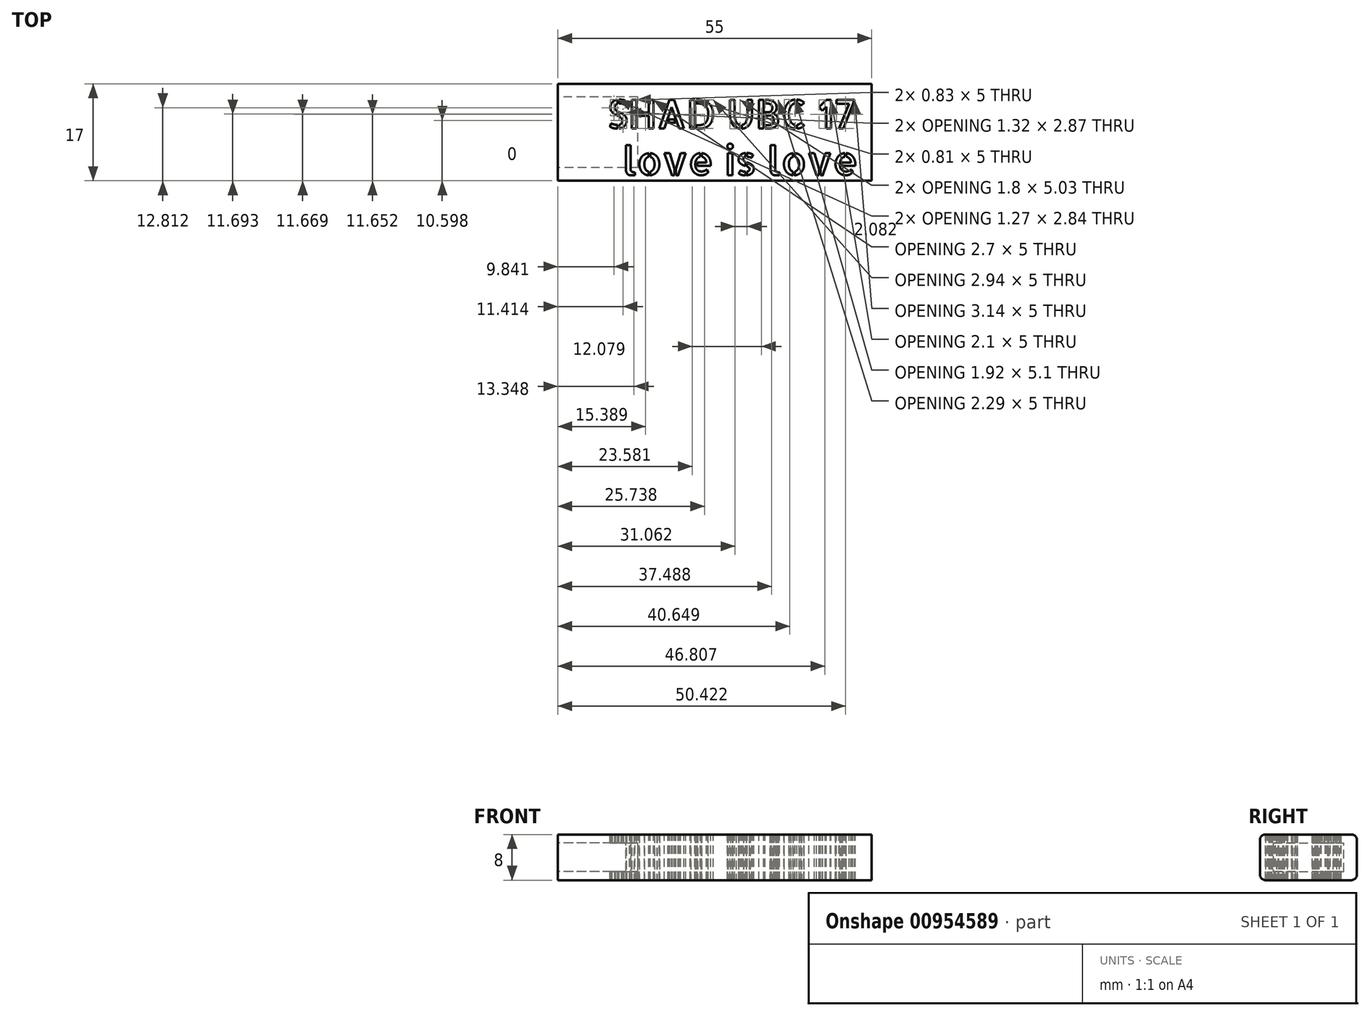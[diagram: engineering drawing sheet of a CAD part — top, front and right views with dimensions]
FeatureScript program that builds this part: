
annotation { "Feature Type Name" : "Feature", "Feature Type Description" : "" }
export const myFeature = defineFeature(function(context is Context, id is Id, definition is map)
    precondition{}
    {
        {
            var Q0;
            Q0=qCreatedBy(makeId("Front.planeOp"),FACE);
            var sketch = newSketch(context, id + "F0", { "sketchPlane" : qUnion([Q0])});
            skPoint(sketch, "E0.middle", {"position": v(0, 0) * mm});
            skLineSegment(sketch, "E1.bottom", {"start": v(7.5, 4) * mm, "end": v(-7.5, 4) * mm});
            skLineSegment(sketch, "E1.top", {"start": v(7.5, -4) * mm, "end": v(-7.5, -4) * mm});
            skLineSegment(sketch, "E1.left", {"start": v(8.5, 3) * mm, "end": v(8.5, -3) * mm});
            skLineSegment(sketch, "E1.right", {"start": v(-8.5, 3) * mm, "end": v(-8.5, -3) * mm});
            skPoint(sketch, "E2.visualSharp", {"position": v(-8.5, 4) * mm});
            skArc(sketch, "E2.filletArc", {"start": v(-7.5, 4) * mm, "mid": v(-8.2, 3.7) * mm, "end": v(-8.5, 3) * mm});
            skPoint(sketch, "E3.visualSharp", {"position": v(-8.5, -4) * mm});
            skArc(sketch, "E3.filletArc", {"start": v(-8.5, -3) * mm, "mid": v(-8.2, -3.7) * mm, "end": v(-7.5, -4) * mm});
            skPoint(sketch, "E4.visualSharp", {"position": v(8.5, -4) * mm});
            skArc(sketch, "E4.filletArc", {"start": v(7.5, -4) * mm, "mid": v(8.2, -3.7) * mm, "end": v(8.5, -3) * mm});
            skPoint(sketch, "E5.visualSharp", {"position": v(8.5, 4) * mm});
            skArc(sketch, "E5.filletArc", {"start": v(8.5, 3) * mm, "mid": v(8.2, 3.7) * mm, "end": v(7.5, 4) * mm});
            skSolve(sketch);
        }
        {
            var Q0;
            Q0 = qSketchRegion(id + "F0", true);
            extrude(context, id + "F1", {"entities" : qUnion([Q0]), "depth" : 55 * mm, "offsetDistance" : 25 * mm});
        }
        {
            var Q0;
            Q0=makeQuery(id+"F1.opExtrude","CAP_FACE",FACE,{"disambiguationData":[OSD([sQuery(id+"F0.wireOp",EDGE,"E1.bottom"),sQuery(id+"F0.wireOp",EDGE,"E1.top"),sQuery(id+"F0.wireOp",EDGE,"E1.left"),sQuery(id+"F0.wireOp",EDGE,"E1.right"),sQuery(id+"F0.wireOp",EDGE,"E2.filletArc"),sQuery(id+"F0.wireOp",EDGE,"E3.filletArc"),sQuery(id+"F0.wireOp",EDGE,"E4.filletArc"),sQuery(id+"F0.wireOp",EDGE,"E5.filletArc")])],"isStart":false});
            var sketch = newSketch(context, id + "F2", { "sketchPlane" : qUnion([Q0])});
            skLineSegment(sketch, "E6.bottom", {"start": v(6.2, -2.5) * mm, "end": v(-6.2, -2.5) * mm});
            skLineSegment(sketch, "E6.top", {"start": v(6.2, 2.5) * mm, "end": v(-6.2, 2.5) * mm});
            skLineSegment(sketch, "E6.left", {"start": v(6.2, -2.5) * mm, "end": v(6.2, 2.5) * mm});
            skLineSegment(sketch, "E6.right", {"start": v(-6.2, -2.5) * mm, "end": v(-6.2, 2.5) * mm});
            skPoint(sketch, "E6.middle", {"position": v(0, 0) * mm});
            skSolve(sketch);
        }
        {
            var Q0;
            Q0 = qSketchRegion(id + "F2", true);
            extrude(context, id + "F3", {"entities" : qUnion([Q0]), "operationType" : NewBodyOperationType.REMOVE, "oppositeDirection" : true, "depth" : 14 * mm, "offsetDistance" : 25 * mm});
        }
        {
            var Q0;
            Q0=makeQuery(id+"F1.opExtrude","SWEPT_BODY",BODY,{"disambiguationData":[OSD([sQuery(id+"F0.wireOp",EDGE,"E1.bottom"),sQuery(id+"F0.wireOp",EDGE,"E1.top"),sQuery(id+"F0.wireOp",EDGE,"E1.left"),sQuery(id+"F0.wireOp",EDGE,"E1.right"),sQuery(id+"F0.wireOp",EDGE,"E2.filletArc"),sQuery(id+"F0.wireOp",EDGE,"E3.filletArc"),sQuery(id+"F0.wireOp",EDGE,"E4.filletArc"),sQuery(id+"F0.wireOp",EDGE,"E5.filletArc")])]});
            var Q1;
            Q1=sQuery(id+"F0.wireOp",EDGE,"E1.left");
            transform(context, id + "F4", {"entities" : qUnion([Q0]), "transformType" : TransformType.ROTATION, "transformAxis" : qUnion([Q1]), "angle" : 90 * degree, "makeCopy" : false});
        }
        {
            var Q0;
            Q0=makeQuery(id+"F1.opExtrude","SWEPT_FACE",FACE,{"disambiguationData":[OSD([sQuery(id+"F0.wireOp",EDGE,"E1.bottom")])]});
            var sketch = newSketch(context, id + "F5", { "sketchPlane" : qUnion([Q0])});
            skText(sketch, "E7", { "text": "love is love", "fontName": "AllertaStencil-Regular.ttf"});
            skText(sketch, "E8", { "text": "SHAD UBC 17", "fontName": "AllertaStencil-Regular.ttf"});
            const initialGuessF5  = {"E7": [-0.03516, 0.001, 1, 0, 0.005], "E8": [-0.03788, 0.00917, 1, 0, 0.005]};
            skSetInitialGuess(sketch, initialGuessF5);
            skSolve(sketch);
        }
        {
            var Q0;
            Q0 = qSketchRegion(id + "F5", true);
            extrude(context, id + "F6", {"entities" : qUnion([Q0]), "operationType" : NewBodyOperationType.REMOVE, "oppositeDirection" : true, "depth" : 25 * mm, "offsetDistance" : 25 * mm});
        }
    });
